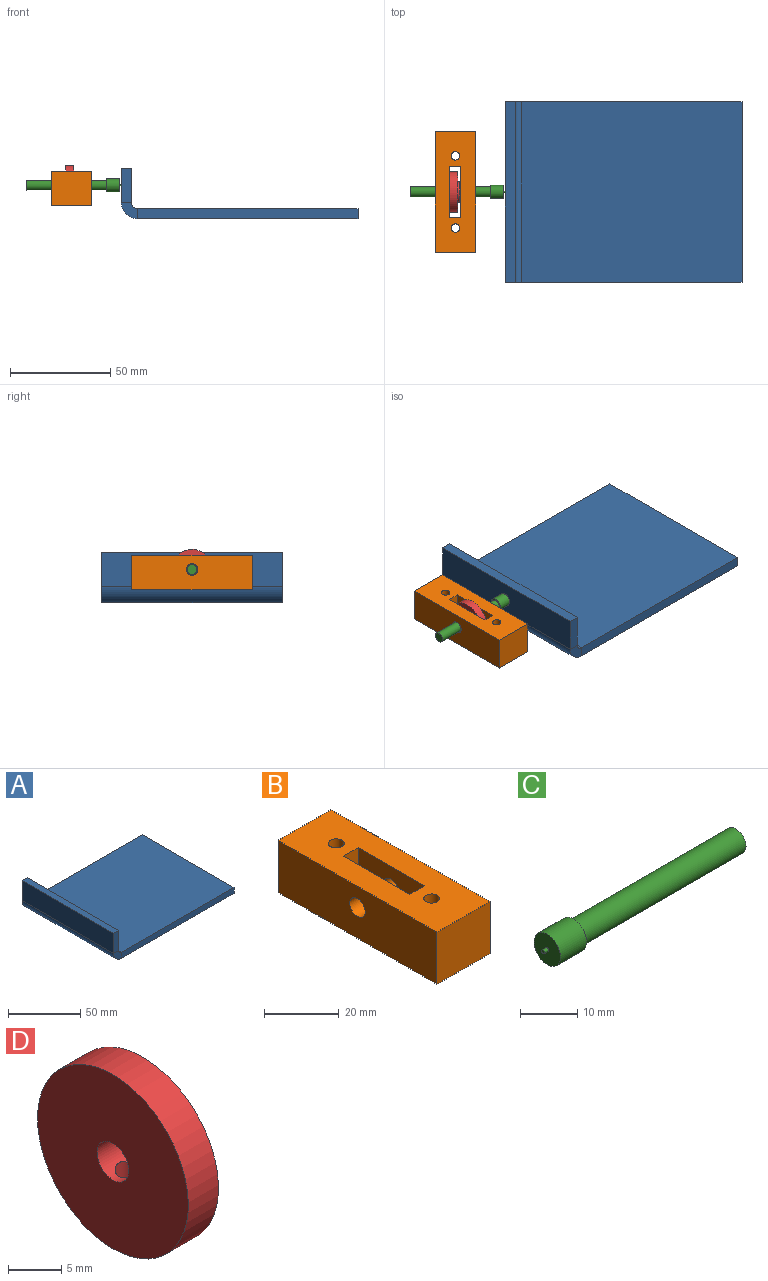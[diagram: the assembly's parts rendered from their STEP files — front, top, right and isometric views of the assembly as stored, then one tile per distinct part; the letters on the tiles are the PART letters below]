
ASSEMBLY  parts=4 mates=4
PART A: 14 faces, bbox 118x90x25 mm
  f0: plane 110x5mm, normal (0,1,0), area 550mm2, adj f1,f3,f4,f11
  f1: plane 90x5mm, normal (1,0,0), area 450mm2, adj f0,f2,f3,f4
  f2: plane 110x5mm, normal (0,-1,0), area 550mm2, adj f1,f3,f4,f10
  f3: plane 110x90mm, normal (0,0,-1), area 9900mm2, adj f0,f1,f2,f12
  f4: plane 110x90mm, normal (0,0,1), area 9900mm2, adj f0,f1,f2,f13
  f5: plane 90x5mm, normal (0,0,1), area 450mm2, adj f6,f7,f8,f9
  f6: plane 17x5mm, normal (0,1,0), area 85mm2, adj f5,f8,f9,f11
  f7: plane 17x5mm, normal (0,-1,0), area 85mm2, adj f5,f8,f9,f10
  f8: plane 90x17mm, normal (-1,0,0), area 1530mm2, adj f5,f6,f7,f12
  f9: plane 90x17mm, normal (1,0,0), area 1530mm2, adj f5,f6,f7,f13
  f10: plane 8x8mm, normal (0,-1,0), area 43.2mm2, adj f2,f7,f12,f13
  f11: plane 8x8mm, normal (0,1,0), area 43.2mm2, adj f0,f6,f12,f13
  f12: cylinder r=8mm len=90mm, axis (0,-1,0), area 1131mm2, adj f3,f8,f10,f11
  f13: cylinder r=3mm len=90mm, axis (0,-1,0), area 424.1mm2, adj f4,f9,f10,f11
PART B: 14 faces, bbox 20x60x17 mm
  f0: plane 60x20mm, normal (0,0,1), area 1034.8mm2, adj f3,f4,f5,f6,f7,f8,f10,f11
  f1: plane 60x20mm, normal (0,0,-1), area 1034.8mm2, adj f3,f4,f5,f6,f7,f8,f10,f11
  f2: cylinder r=2.9mm len=7.25mm, axis (-1,0,0), area 132.1mm2, adj f3,f12
  f3: plane 60x17mm, normal (1,0,0), area 993.6mm2, adj f0,f1,f2,f4,f6
  f4: plane 20x17mm, normal (0,1,0), area 340mm2, adj f0,f1,f3,f5
  f5: plane 60x17mm, normal (-1,0,0), area 993.6mm2, adj f0,f1,f4,f6,f9
  f6: plane 20x17mm, normal (0,-1,0), area 340mm2, adj f0,f1,f3,f5
  f7: cylinder r=2.1mm len=17mm, axis (0,0,1), area 224.3mm2, adj f0,f1
  f8: cylinder r=2.1mm len=17mm, axis (0,0,1), area 224.3mm2, adj f0,f1
  f9: cylinder r=2.9mm len=7.25mm, axis (-1,0,0), area 132.1mm2, adj f5,f13
  f10: plane 17x5.5mm, normal (0,-1,0), area 93.5mm2, adj f0,f1,f12,f13
  f11: plane 17x5.5mm, normal (0,1,0), area 93.5mm2, adj f0,f1,f12,f13
  f12: plane 25x17mm, normal (-1,0,0), area 398.6mm2, adj f0,f1,f2,f10,f11
  f13: plane 25x17mm, normal (1,0,0), area 398.6mm2, adj f0,f1,f9,f10,f11
PART C: 7 faces, bbox 47.5x6.5x6.5 mm
  f0: plane 5x5mm, normal (1,0,0), area 19.6mm2, adj f1
  f1: cylinder r=2.5mm len=40mm, axis (1,0,0), area 628.3mm2, adj f0,f2
  f2: plane 6.5x6.5mm, normal (1,0,0), area 13.5mm2, adj f1,f3
  f3: cylinder r=3.25mm len=6.5mm, axis (1,0,0), area 132.7mm2, adj f2,f4
  f4: plane 6.5x6.5mm, normal (-1,0,0), area 32.7mm2, adj f3,f5
  f5: cylinder r=0.38mm len=1mm, axis (1,0,0), area 2.4mm2, adj f4,f6
  f6: plane 0.75x0.75mm, normal (-1,0,0), area 0.4mm2, adj f5
PART D: 7 faces, bbox 5x20x20 mm
  f0: cylinder r=10mm len=20mm, axis (1,0,0), area 246.8mm2, adj f2,f5,f6
  f1: cylinder r=2.1mm len=5mm, axis (-1,0,0), area 61.2mm2, adj f2,f3,f6
  f2: plane 20x20mm, normal (-1,0,0), area 300.3mm2, adj f0,f1
  f3: plane 10x10mm, normal (1,0,0), area 64.7mm2, adj f1,f4
  f4: cylinder r=5mm len=10mm, axis (1,0,0), area 31.4mm2, adj f3,f5
  f5: plane 20x20mm, normal (1,0,0), area 235.6mm2, adj f0,f4
  f6: cylinder r=1.2mm len=8.28mm, axis (0,0,1), area 60.7mm2, adj f0,f1
PLACE A at identity fixed
PLACE B t=(-83.83,0,6.5)mm
PLACE C rot(axis=(0,1,0),180deg) t=(-59,0,16.5)mm
PLACE D rot(axis=(1,0,0),34.6deg) t=(-86.58,0,16.5)mm
MATE fastened C.f1 <-> A.f8  axis (-1,0,0) through (-59,0,16.5)mm
MATE cylindrical D.f0 <-> C.f1  axis (-1,0,0) through (-86.58,0,16.5)mm
MATE slider B.f2 <-> C.f1  axis (-1,0,0) through (-93.83,0,16.5)mm
MATE planar D.f0 <-> B.f13  axis (-1,0,0) through (-86.58,0,16.5)mm
